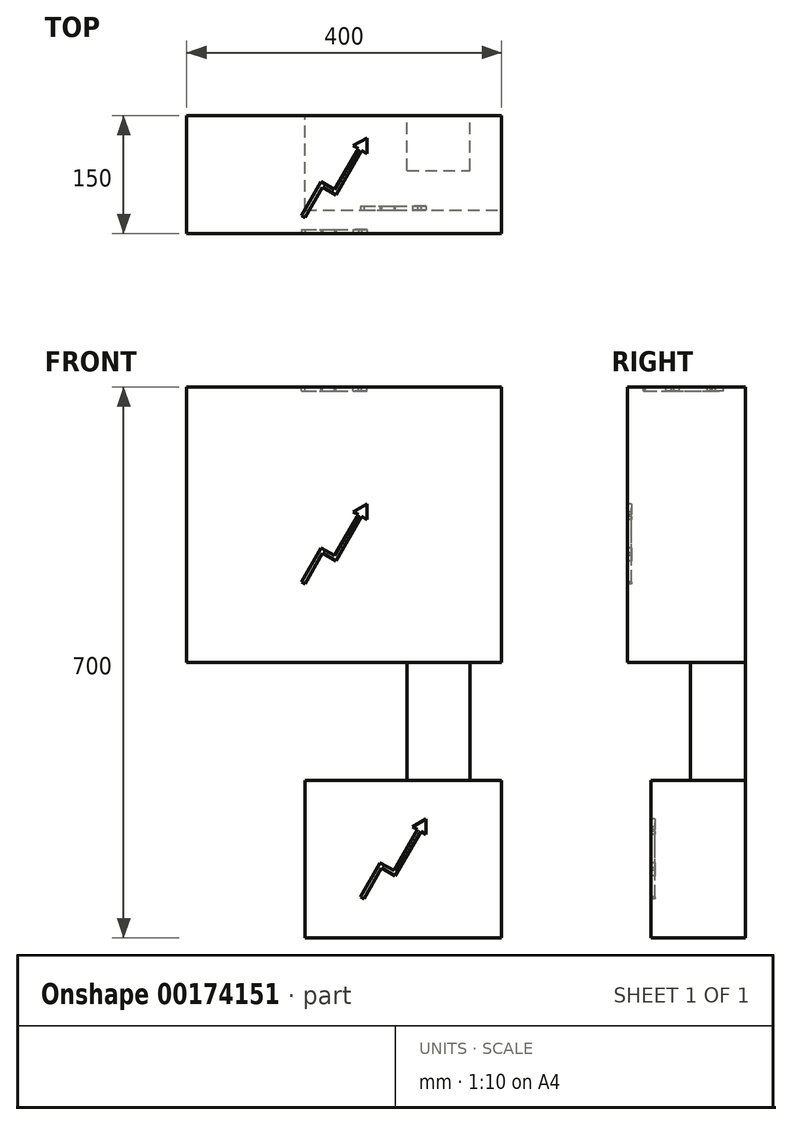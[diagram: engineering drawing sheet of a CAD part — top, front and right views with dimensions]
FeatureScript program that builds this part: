
annotation { "Feature Type Name" : "Feature", "Feature Type Description" : "" }
export const myFeature = defineFeature(function(context is Context, id is Id, definition is map)
    precondition{}
    {
        {
            var Q0;
            Q0=qCreatedBy(makeId("Front.planeOp"),FACE);
            var sketch = newSketch(context, id + "F0", { "sketchPlane" : qUnion([Q0])});
            skLineSegment(sketch, "E0.bottom", {"start": v(0, 0) * mm, "end": v(400, 0) * mm});
            skLineSegment(sketch, "E0.top", {"start": v(0, 350) * mm, "end": v(400, 350) * mm});
            skLineSegment(sketch, "E0.left", {"start": v(0, 0) * mm, "end": v(0, 350) * mm});
            skLineSegment(sketch, "E0.right", {"start": v(400, 0) * mm, "end": v(400, 350) * mm});
            skSolve(sketch);
        }
        {
            var Q0;
            Q0=makeQuery(id+"F0.imprint","IMPRINT",FACE,{"disambiguationData":[TD([[makeQuery(id+"F0.imprint","IMPRINT",EDGE,{"derivedFrom":sQuery(id+"F0.wireOp",EDGE,"E0.bottom")}),1.0]])]});
            var Q1;
            Q1=makeQuery(id+"F0.imprint","IMPRINT",FACE,{"disambiguationData":[TD([[makeQuery(id+"F0.imprint","IMPRINT",EDGE,{"derivedFrom":sQuery(id+"F0.wireOp",EDGE,"Th4niw2f-hRjs-mVe2-G7W7-12X1Qeb7SmW6.bottom")}),-1.0]])]});
            extrude(context, id + "F1", {"entities" : qUnion([Q0, Q1]), "depth" : 150 * mm});
        }
        {
            var Q0;
            Q0=makeQuery(id+"F1.opExtrude","SWEPT_FACE",FACE,{"disambiguationData":[OSD([sQuery(id+"F0.wireOp",EDGE,"E0.top")])]});
            var sketch = newSketch(context, id + "F2", { "sketchPlane" : qUnion([Q0])});
            skLineSegment(sketch, "E1", {"start": v(145.67, -127.5) * mm, "end": v(170.67, -84.2) * mm});
            skLineSegment(sketch, "E2", {"start": v(170.67, -84.2) * mm, "end": v(188, -94.2) * mm});
            skLineSegment(sketch, "E3", {"start": v(188, -94.2) * mm, "end": v(218, -42.24) * mm});
            skLineSegment(sketch, "E4.0", {"start": v(189.82, -101.03) * mm, "end": v(222.32, -44.74) * mm});
            skLineSegment(sketch, "E4.1", {"start": v(172.5, -91.03) * mm, "end": v(189.82, -101.03) * mm});
            skLineSegment(sketch, "E4.2", {"start": v(150, -130) * mm, "end": v(172.5, -91.03) * mm});
            skLineSegment(sketch, "E5", {"start": v(211.5, -38.49) * mm, "end": v(218, -42.24) * mm});
            skLineSegment(sketch, "E6", {"start": v(228.82, -48.49) * mm, "end": v(228.82, -28.49) * mm});
            skLineSegment(sketch, "E7", {"start": v(228.82, -28.49) * mm, "end": v(211.5, -38.49) * mm});
            skLineSegment(sketch, "E8", {"start": v(145.67, -127.5) * mm, "end": v(150, -130) * mm});
            skLineSegment(sketch, "E9.trimOffspring", {"start": v(222.32, -44.74) * mm, "end": v(228.82, -48.49) * mm});
            skSolve(sketch);
        }
        {
            var Q0;
            Q0=makeQuery(id+"F2.imprint","IMPRINT",FACE,{"disambiguationData":[TD([[makeQuery(id+"F2.imprint","IMPRINT",EDGE,{"derivedFrom":sQuery(id+"F2.wireOp",EDGE,"E1")}),-1.0]])]});
            extrude(context, id + "F3", {"entities" : qUnion([Q0]), "operationType" : NewBodyOperationType.REMOVE, "oppositeDirection" : true, "depth" : 5 * mm});
        }
        {
            var Q0;
            Q0=makeQuery(id+"F1.opExtrude","CAP_FACE",FACE,{"disambiguationData":[OSD([sQuery(id+"F0.wireOp",EDGE,"E0.bottom"),sQuery(id+"F0.wireOp",EDGE,"E0.top"),sQuery(id+"F0.wireOp",EDGE,"E0.left"),sQuery(id+"F0.wireOp",EDGE,"E0.right")])],"isStart":false});
            var sketch = newSketch(context, id + "F4", { "sketchPlane" : qUnion([Q0])});
            skLineSegment(sketch, "E10", {"start": v(145.67, 102.5) * mm, "end": v(170.67, 145.8) * mm});
            skLineSegment(sketch, "E11", {"start": v(170.67, 145.8) * mm, "end": v(188, 135.8) * mm});
            skLineSegment(sketch, "E12", {"start": v(188, 135.8) * mm, "end": v(218, 187.76) * mm});
            skLineSegment(sketch, "E13.0", {"start": v(189.82, 128.97) * mm, "end": v(222.32, 185.26) * mm});
            skLineSegment(sketch, "E13.1", {"start": v(172.5, 138.97) * mm, "end": v(189.82, 128.97) * mm});
            skLineSegment(sketch, "E13.2", {"start": v(150, 100) * mm, "end": v(172.5, 138.97) * mm});
            skLineSegment(sketch, "E14", {"start": v(211.5, 191.51) * mm, "end": v(218, 187.76) * mm});
            skLineSegment(sketch, "E15", {"start": v(228.82, 181.51) * mm, "end": v(228.82, 201.51) * mm});
            skLineSegment(sketch, "E16", {"start": v(228.82, 201.51) * mm, "end": v(211.5, 191.51) * mm});
            skLineSegment(sketch, "E17", {"start": v(145.67, 102.5) * mm, "end": v(150, 100) * mm});
            skLineSegment(sketch, "E18.trimOffspring", {"start": v(222.32, 185.26) * mm, "end": v(228.82, 181.51) * mm});
            skSolve(sketch);
        }
        {
            var Q0;
            Q0=makeQuery(id+"F4.imprint","IMPRINT",FACE,{"disambiguationData":[TD([[makeQuery(id+"F4.imprint","IMPRINT",EDGE,{"derivedFrom":sQuery(id+"F4.wireOp",EDGE,"E10")}),-1.0]])]});
            extrude(context, id + "F5", {"entities" : qUnion([Q0]), "operationType" : NewBodyOperationType.REMOVE, "oppositeDirection" : true, "depth" : 5 * mm});
        }
        {
            var Q0;
            Q0=qCreatedBy(makeId("Front.planeOp"),FACE);
            var sketch = newSketch(context, id + "F6", { "sketchPlane" : qUnion([Q0])});
            skLineSegment(sketch, "E19.bottom", {"start": v(280, 0) * mm, "end": v(360, 0) * mm});
            skLineSegment(sketch, "E19.top", {"start": v(280, -150) * mm, "end": v(360, -150) * mm});
            skLineSegment(sketch, "E19.left", {"start": v(280, 0) * mm, "end": v(280, -150) * mm});
            skLineSegment(sketch, "E19.right", {"start": v(360, 0) * mm, "end": v(360, -150) * mm});
            skSolve(sketch);
        }
        {
            var Q0;
            Q0=makeQuery(id+"F6.imprint","IMPRINT",FACE,{"disambiguationData":[TD([[makeQuery(id+"F6.imprint","IMPRINT",EDGE,{"derivedFrom":sQuery(id+"F6.wireOp",EDGE,"E19.bottom")}),-1.0]])]});
            extrude(context, id + "F7", {"entities" : qUnion([Q0]), "operationType" : NewBodyOperationType.ADD, "depth" : 70 * mm});
        }
        {
            var Q0;
            Q0=qCreatedBy(makeId("Front.planeOp"),FACE);
            var sketch = newSketch(context, id + "F8", { "sketchPlane" : qUnion([Q0])});
            skLineSegment(sketch, "E20.bottom", {"start": v(150, -150) * mm, "end": v(400, -150) * mm});
            skLineSegment(sketch, "E20.top", {"start": v(150, -350) * mm, "end": v(400, -350) * mm});
            skLineSegment(sketch, "E20.left", {"start": v(150, -150) * mm, "end": v(150, -350) * mm});
            skLineSegment(sketch, "E20.right", {"start": v(400, -150) * mm, "end": v(400, -350) * mm});
            skSolve(sketch);
        }
        {
            var Q0;
            Q0=makeQuery(id+"F8.imprint","IMPRINT",FACE,{"disambiguationData":[TD([[makeQuery(id+"F8.imprint","IMPRINT",EDGE,{"derivedFrom":sQuery(id+"F8.wireOp",EDGE,"E20.bottom")}),-1.0]])]});
            extrude(context, id + "F9", {"entities" : qUnion([Q0]), "operationType" : NewBodyOperationType.ADD, "depth" : 120 * mm});
        }
        {
            var Q0;
            Q0=makeQuery(id+"F9.opExtrude","CAP_FACE",FACE,{"disambiguationData":[OSD([sQuery(id+"F8.wireOp",EDGE,"E20.bottom"),sQuery(id+"F8.wireOp",EDGE,"E20.top"),sQuery(id+"F8.wireOp",EDGE,"E20.left"),sQuery(id+"F8.wireOp",EDGE,"E20.right")])],"isStart":false});
            var sketch = newSketch(context, id + "F10", { "sketchPlane" : qUnion([Q0])});
            skLineSegment(sketch, "E21", {"start": v(220.67, -297.5) * mm, "end": v(245.67, -254.2) * mm});
            skLineSegment(sketch, "E22", {"start": v(245.67, -254.2) * mm, "end": v(263, -264.2) * mm});
            skLineSegment(sketch, "E23", {"start": v(263, -264.2) * mm, "end": v(293, -212.24) * mm});
            skLineSegment(sketch, "E24.0", {"start": v(264.82, -271.03) * mm, "end": v(297.32, -214.74) * mm});
            skLineSegment(sketch, "E24.1", {"start": v(247.5, -261.03) * mm, "end": v(264.82, -271.03) * mm});
            skLineSegment(sketch, "E24.2", {"start": v(225, -300) * mm, "end": v(247.5, -261.03) * mm});
            skLineSegment(sketch, "E25", {"start": v(286.5, -208.49) * mm, "end": v(293, -212.24) * mm});
            skLineSegment(sketch, "E26", {"start": v(303.82, -218.49) * mm, "end": v(303.82, -198.49) * mm});
            skLineSegment(sketch, "E27", {"start": v(303.82, -198.49) * mm, "end": v(286.5, -208.49) * mm});
            skLineSegment(sketch, "E28", {"start": v(220.67, -297.5) * mm, "end": v(225, -300) * mm});
            skLineSegment(sketch, "E29.trimOffspring", {"start": v(297.32, -214.74) * mm, "end": v(303.82, -218.49) * mm});
            skSolve(sketch);
        }
        {
            var Q0;
            Q0=makeQuery(id+"F10.imprint","IMPRINT",FACE,{"disambiguationData":[TD([[makeQuery(id+"F10.imprint","IMPRINT",EDGE,{"derivedFrom":sQuery(id+"F10.wireOp",EDGE,"E21")}),-1.0]])]});
            extrude(context, id + "F11", {"entities" : qUnion([Q0]), "operationType" : NewBodyOperationType.REMOVE, "oppositeDirection" : true, "depth" : 5 * mm});
        }
    });
